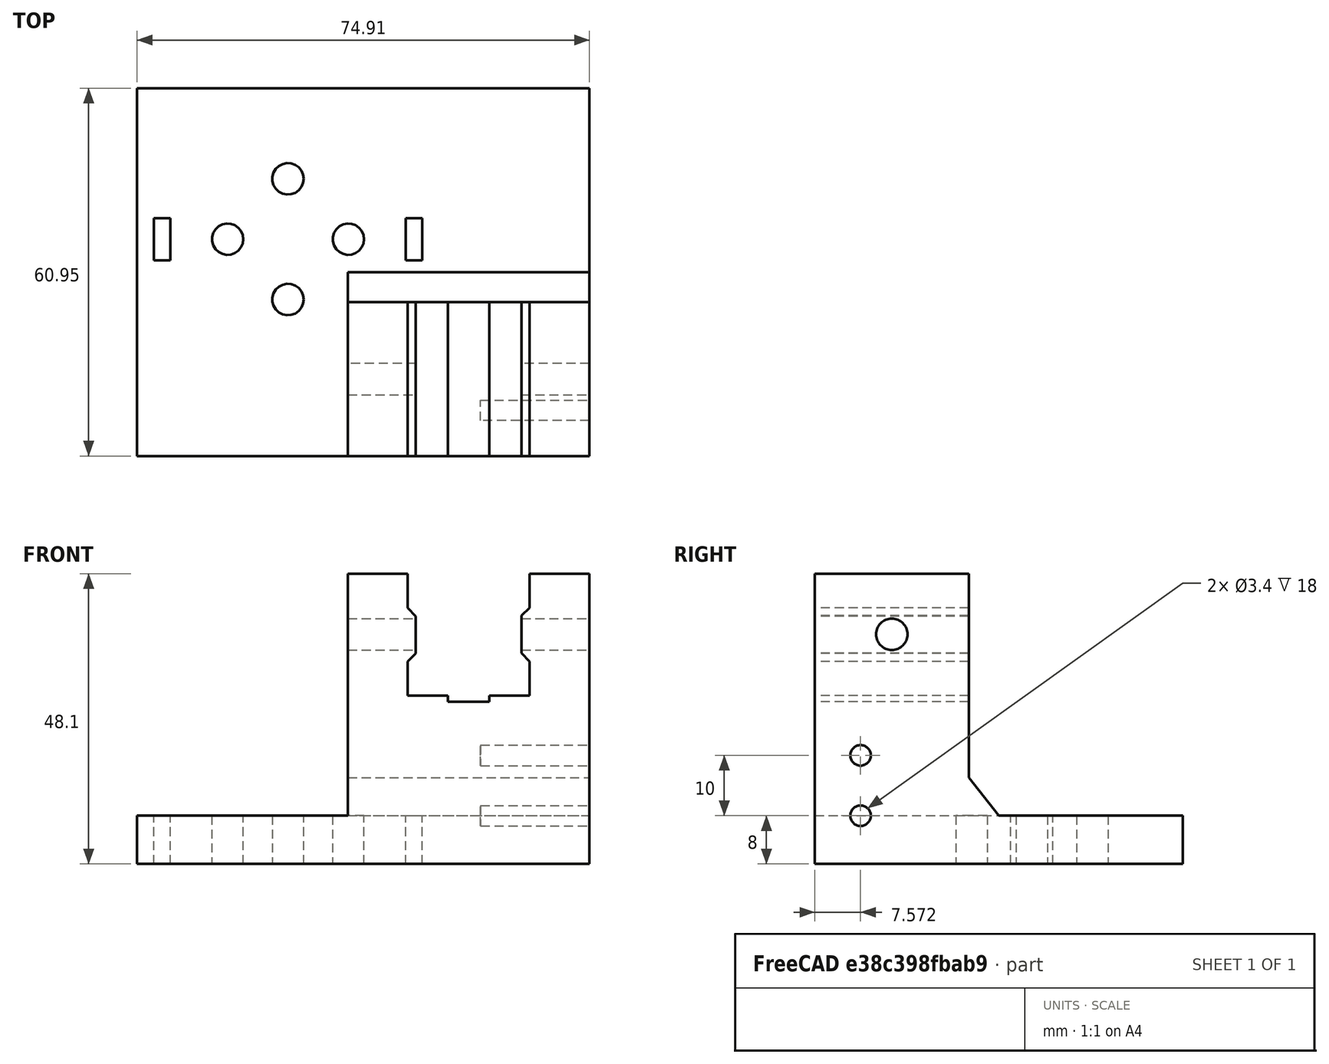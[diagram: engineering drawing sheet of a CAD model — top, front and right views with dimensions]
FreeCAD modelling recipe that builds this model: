
FCSTD DOCUMENT  (FreeCAD 1.0R39109 (Git))
Label: plotter_x_axis_idler
License: All rights reserved
LicenseURL: https://en.wikipedia.org/wiki/All_rights_reserved
objects: Sketcher::SketchObject×12, PartDesign::Pad×3, PartDesign::Pocket×3, PartDesign::Body×2, Mesh::Feature×1, PartDesign::LinearPattern×1, Part::Mirroring×1, PartDesign::FeatureBase×1
note: 49 computed .brp shape members not serialized (recipe doc carries the construction recipe); baked Part::Feature solids carry a one-line shape summary decoded from their .brp

FEATURE [Mesh::Feature] _0x20_v_slot  label="20x20_v-slot"
  Placement = pos=(29.9,-56,38) rot=(0,0,1;0rad)
FEATURE [Sketcher::SketchObject] Sketch007
  ArcFitTolerance = 1e-06
  AttachmentSupport = -> [XY_Plane001]
  FullyConstrained = false
  MakeInternals = false
  MapMode = 5
  sketch-geometry (19):
    g0: LineSegment StartX=49.9144 StartY=35.9499 StartZ=0 EndX=-25 EndY=35.9499 EndZ=0
    g1: LineSegment StartX=-25 StartY=35.9499 StartZ=0 EndX=-25 EndY=-25 EndZ=0
    g2: LineSegment StartX=-25 StartY=-25 StartZ=0 EndX=49.9144 EndY=-25 EndZ=0
    g3: LineSegment StartX=49.9144 StartY=-25 StartZ=0 EndX=49.9144 EndY=35.9499 EndZ=0
    g4: Circle CenterX=0 CenterY=10 CenterZ=0 NormalX=0 NormalY=0 NormalZ=1 AngleXU=0 Radius=2.6
    g5: Circle CenterX=10 CenterY=0 CenterZ=0 NormalX=0 NormalY=0 NormalZ=1 AngleXU=0 Radius=2.6
    g6: Circle CenterX=-10 CenterY=0 CenterZ=0 NormalX=0 NormalY=0 NormalZ=1 AngleXU=0 Radius=2.6
    g7: Circle CenterX=0 CenterY=-10 CenterZ=0 NormalX=0 NormalY=0 NormalZ=1 AngleXU=0 Radius=2.6
    g8: LineSegment [constr] StartX=43.4104 StartY=34.4675 StartZ=0 EndX=43.4104 EndY=14.8633 EndZ=0
    g9: LineSegment StartX=22.25 StartY=-3.5 StartZ=0 EndX=22.25 EndY=3.5 EndZ=0
    g10: LineSegment StartX=22.25 StartY=3.5 StartZ=0 EndX=19.5 EndY=3.5 EndZ=0
    g11: LineSegment StartX=19.5 StartY=3.5 StartZ=0 EndX=19.5 EndY=-3.5 EndZ=0
    g12: LineSegment StartX=19.5 StartY=-3.5 StartZ=0 EndX=22.25 EndY=-3.5 EndZ=0
    g13: GeomPoint [constr] X=20.875 Y=0 Z=0
    g14: LineSegment StartX=-19.5 StartY=-3.5 StartZ=0 EndX=-19.5 EndY=3.5 EndZ=0
    g15: LineSegment StartX=-19.5 StartY=3.5 StartZ=0 EndX=-22.25 EndY=3.5 EndZ=0
    g16: LineSegment StartX=-22.25 StartY=3.5 StartZ=0 EndX=-22.25 EndY=-3.5 EndZ=0
    g17: LineSegment StartX=-22.25 StartY=-3.5 StartZ=0 EndX=-19.5 EndY=-3.5 EndZ=0
    g18: GeomPoint [constr] X=-20.875 Y=0 Z=0
  constraints (49):
    c: Coincident(g0,g1)
    c: Coincident(g1,g2)
    c: Coincident(g2,g3)
    c: Coincident(g3,g0)
    c: Horizontal(g0)
    c: Horizontal(g2)
    c: Vertical(g1)
    c: Vertical(g3)
    c: Diameter(g4) = 5.2
    c: PointOnObject(g4,g-2)
    c: Diameter(g5) = 5.2
    c: PointOnObject(g5,g-1)
    c: Diameter(g6) = 5.2
    c: Diameter(g7) = 5.2
    c: PointOnObject(g7,g-2)
    c: DistanceX(g-1,g5) = 10
    c: DistanceY(g7,g-1) = 10
    c: DistanceY(g-1,g4) = 10
    c: DistanceX(g6,g-1) = 10
    c: PointOnObject(g6,g-1)
    c: Vertical(g8)
    c: DistanceY(g1,g-1) = 25
    c: DistanceX(g1,g-1) = 25
    c: Coincident(g9,g10)
    c: Coincident(g10,g11)
    c: Coincident(g11,g12)
    c: Coincident(g12,g9)
    c: Vertical(g9)
    c: Vertical(g11)
    c: Horizontal(g10)
    c: Horizontal(g12)
    c: Symmetric(g11,g9,g13)
    c: PointOnObject(g13,g-1)
    c: Coincident(g14,g15)
    c: Coincident(g15,g16)
    c: Coincident(g16,g17)
    c: Coincident(g17,g14)
    c: Vertical(g14)
    c: Vertical(g16)
    c: Horizontal(g15)
    c: Horizontal(g17)
    c: Symmetric(g16,g14,g18)
    c: PointOnObject(g18,g-1)
    c: Equal(g11,g14)
    c: DistanceY(g11,g11) = 7
    c: Equal(g10,g15)
    c: DistanceX(g15,g15) = 2.75
    c: DistanceX(g14,g11) = 39
    c: DistanceX(g14,g-1) = 19.5
FEATURE [PartDesign::Pad] Pad005
  Direction = (0,0,1)
  Length = 8
  Length2 = 10
  Profile = -> Sketch007
  ReferenceAxis = -> Sketch007 [N_Axis]
  Refine = true
  Suppressed = false
  Type = 0
FEATURE [Sketcher::SketchObject] Sketch009
  ArcFitTolerance = 1e-06
  AttachmentSupport = -> [Pad005]
  ExternalGeometry = -> [Pad005]
  FullyConstrained = false
  MakeInternals = false
  MapMode = 5
  Placement = pos=(0,0,8) rot=(0,0,1;0rad)
  sketch-geometry (4):
    g0: LineSegment StartX=49.9144 StartY=35.9499 StartZ=0 EndX=9.91437 EndY=35.9499 EndZ=0
    g1: LineSegment StartX=9.91437 StartY=35.9499 StartZ=0 EndX=9.91437 EndY=10.4651 EndZ=0
    g2: LineSegment StartX=9.91437 StartY=10.4651 StartZ=0 EndX=49.9144 EndY=10.4651 EndZ=0
    g3: LineSegment StartX=49.9144 StartY=10.4651 StartZ=0 EndX=49.9144 EndY=35.9499 EndZ=0
  constraints (10):
    c: Coincident(g0,g1)
    c: Coincident(g1,g2)
    c: Coincident(g2,g3)
    c: Coincident(g3,g0)
    c: Horizontal(g0)
    c: Horizontal(g2)
    c: Vertical(g1)
    c: Vertical(g3)
    c: Distance(g1,g3) = 40
    c: Coincident(g0,g-4)
FEATURE [PartDesign::Pad] Pad006
  BaseFeature = -> Pad005
  Direction = (0,0,1)
  Length = 40.1
  Length2 = 10
  Profile = -> Sketch009
  ReferenceAxis = -> Sketch009 [N_Axis]
  Refine = true
  Suppressed = false
  Type = 0
FEATURE [Sketcher::SketchObject] Sketch010
  ArcFitTolerance = 1e-06
  AttachmentSupport = -> [Pad006]
  ExternalGeometry = -> [Pad006]
  FullyConstrained = false
  MakeInternals = false
  MapMode = 5
  Placement = pos=(0,10.4651,0) rot=(1,0,0;1.5708rad)
  sketch-geometry (17):
    g0: LineSegment [constr] StartX=29.9144 StartY=48.1 StartZ=0 EndX=29.9144 EndY=14.8286 EndZ=0
    g1: LineSegment StartX=19.8144 StartY=48.1 StartZ=0 EndX=19.8144 EndY=42.4266 EndZ=0
    g2: LineSegment StartX=19.8144 StartY=42.4266 StartZ=0 EndX=21.1404 EndY=41.0594 EndZ=0
    g3: LineSegment StartX=21.1404 StartY=41.0594 StartZ=0 EndX=21.1404 EndY=34.8594 EndZ=0
    g4: LineSegment StartX=21.1404 StartY=34.8594 StartZ=0 EndX=19.8144 EndY=33.5734 EndZ=0
    g5: LineSegment StartX=19.8144 StartY=33.5734 StartZ=0 EndX=19.8144 EndY=27.9 EndZ=0
    g6: LineSegment StartX=19.8144 StartY=27.9 StartZ=0 EndX=26.496 EndY=27.9 EndZ=0
    g7: LineSegment StartX=26.496 StartY=27.9 StartZ=0 EndX=26.496 EndY=26.9 EndZ=0
    g8: LineSegment StartX=26.496 StartY=26.9 StartZ=0 EndX=33.3327 EndY=26.9 EndZ=0
    g9: LineSegment StartX=33.3327 StartY=26.9 StartZ=0 EndX=33.3327 EndY=27.9 EndZ=0
    g10: LineSegment StartX=33.3327 StartY=27.9 StartZ=0 EndX=40.0144 EndY=27.9 EndZ=0
    g11: LineSegment StartX=40.0144 StartY=27.9 StartZ=0 EndX=40.0144 EndY=33.5734 EndZ=0
    g12: LineSegment StartX=40.0144 StartY=33.5734 StartZ=0 EndX=38.6893 EndY=34.9653 EndZ=0
    g13: LineSegment StartX=38.6893 StartY=34.9653 StartZ=0 EndX=38.6893 EndY=41.1653 EndZ=0
    g14: LineSegment StartX=38.6893 StartY=41.1653 StartZ=0 EndX=40.0144 EndY=42.4266 EndZ=0
    g15: LineSegment StartX=40.0144 StartY=42.4266 StartZ=0 EndX=40.0144 EndY=48.1 EndZ=0
    g16: LineSegment StartX=40.0144 StartY=48.1 StartZ=0 EndX=19.8144 EndY=48.1 EndZ=0
  constraints (46):
    c: Symmetric(g-3,g-3,g0)
    c: Vertical(g0)
    c: PointOnObject(g1,g-3)
    c: Vertical(g1)
    c: Coincident(g1,g2)
    c: Coincident(g2,g3)
    c: Vertical(g3)
    c: Coincident(g3,g4)
    c: Coincident(g4,g5)
    c: Vertical(g5)
    c: Coincident(g5,g6)
    c: Coincident(g6,g7)
    c: Vertical(g7)
    c: Coincident(g7,g8)
    c: Horizontal(g8)
    c: Coincident(g8,g9)
    c: Vertical(g9)
    c: Coincident(g9,g10)
    c: Coincident(g10,g11)
    c: Vertical(g11)
    c: Coincident(g11,g12)
    c: Coincident(g12,g13)
    c: Vertical(g13)
    c: Coincident(g13,g14)
    c: Coincident(g14,g15)
    c: PointOnObject(g15,g-3)
    c: Vertical(g15)
    c: Coincident(g15,g16)
    c: Coincident(g16,g1)
    c: Equal(g13,g3)
    c: Equal(g15,g1)
    c: Equal(g1,g5)
    c: Equal(g5,g11)
    c: Equal(g6,g10)
    c: Equal(g9,g7)
    c: DistanceY(g3,g3) = 6.2
    c: DistanceX(g4,g11) = 20.2
    c: DistanceX(g11,g14) = 0
    c: DistanceX(g1,g4) = 0
    c: DistanceY(g10,g15) = 20.2
    c: DistanceY(g10,g5) = 0
    c: Parallel(g6,g10)
    c: DistanceY(g9,g9) = 1
    c: DistanceX(g1,g0) = 10.1
    c: Perpendicular(g4,g2)
    c: Perpendicular(g12,g14)
FEATURE [PartDesign::Pocket] Pocket004
  BaseFeature = -> Pad006
  Direction = (0,1,-2e-16)
  Length = 50
  Length2 = 5
  Profile = -> Sketch010
  ReferenceAxis = -> Sketch010 [N_Axis]
  Refine = true
  Suppressed = false
  Type = 0
FEATURE [Sketcher::SketchObject] Sketch011
  ArcFitTolerance = 1e-06
  AttachmentSupport = -> [Pocket004]
  ExternalGeometry = -> [Pocket004]
  FullyConstrained = true
  MakeInternals = false
  MapMode = 5
  Placement = pos=(0,0,8) rot=(0,0,1;0rad)
  sketch-geometry (8):
    g0: LineSegment StartX=15.3144 StartY=10.4651 StartZ=0 EndX=15.3144 EndY=-25 EndZ=0
    g1: LineSegment StartX=15.3144 StartY=-25 StartZ=0 EndX=19.8144 EndY=-25 EndZ=0
    g2: LineSegment StartX=19.8144 StartY=-25 StartZ=0 EndX=19.8144 EndY=-3.5 EndZ=0
    g3: LineSegment StartX=19.8144 StartY=-3.5 StartZ=0 EndX=19.5 EndY=-3.5 EndZ=0
    g4: LineSegment StartX=19.5 StartY=-3.5 StartZ=0 EndX=19.5 EndY=3.5 EndZ=0
    g5: LineSegment StartX=19.5 StartY=3.5 StartZ=0 EndX=19.8144 EndY=3.5 EndZ=0
    g6: LineSegment StartX=19.8144 StartY=3.5 StartZ=0 EndX=19.8144 EndY=10.4651 EndZ=0
    g7: LineSegment StartX=19.8144 StartY=10.4651 StartZ=0 EndX=15.3144 EndY=10.4651 EndZ=0
  constraints (21):
    c: Vertical(g0)
    c: Coincident(g0,g1)
    c: Coincident(g1,g2)
    c: Vertical(g2)
    c: Coincident(g2,g3)
    c: Coincident(g3,g4)
    c: Coincident(g4,g5)
    c: Horizontal(g5)
    c: Coincident(g5,g6)
    c: Vertical(g6)
    c: Coincident(g6,g7)
    c: Coincident(g7,g0)
    c: Coincident(g4,g-3)
    c: Coincident(g3,g-4)
    c: Parallel(g3,g-1)
    c: Equal(g1,g7)
    c: Parallel(g7,g1)
    c: PointOnObject(g1,g-6)
    c: Coincident(g6,g-5)
    c: DistanceY(g0,g-5) = 0
    c: DistanceX(g1,g1) = 4.5
FEATURE [Sketcher::SketchObject] Sketch012
  ArcFitTolerance = 1e-06
  FullyConstrained = false
  MakeInternals = false
  MapMode = 5
  Placement = pos=(49.9144,0,0) rot=(0.57735,0.57735,0.57735;2.0944rad)
  sketch-geometry (1):
    g0: Circle CenterX=28.4297 CenterY=38.1 CenterZ=0 NormalX=0 NormalY=0 NormalZ=1 AngleXU=0 Radius=2.7
  constraints (2):
    c: Diameter(g0) = 5.4
    c: DistanceY(g0,g-3) = 10
FEATURE [Sketcher::SketchObject] Sketch013
  ArcFitTolerance = 1e-06
  FullyConstrained = true
  MakeInternals = false
  MapMode = 5
  Placement = pos=(0,20.8055,0) rot=(1,0,0;1.5708rad)
  sketch-geometry (8):
    g0: LineSegment StartX=40.0144 StartY=48.1 StartZ=0 EndX=40.0144 EndY=42.4266 EndZ=0
    g1: LineSegment StartX=40.0144 StartY=42.4266 StartZ=0 EndX=38.6893 EndY=41.1653 EndZ=0
    g2: LineSegment StartX=38.6893 StartY=41.1653 StartZ=0 EndX=38.6893 EndY=34.9653 EndZ=0
    g3: LineSegment StartX=38.6893 StartY=34.9653 StartZ=0 EndX=40.0144 EndY=33.5734 EndZ=0
    g4: LineSegment StartX=40.0144 StartY=33.5734 StartZ=0 EndX=40.0144 EndY=27.9 EndZ=0
    g5: LineSegment StartX=40.0144 StartY=27.9 StartZ=0 EndX=49.9144 EndY=28.05 EndZ=0
    g6: LineSegment StartX=49.9144 StartY=28.05 StartZ=0 EndX=49.9144 EndY=48.1 EndZ=0
    g7: LineSegment StartX=49.9144 StartY=48.1 StartZ=0 EndX=40.0144 EndY=48.1 EndZ=0
  constraints (16):
    c: Coincident(g-4,g0)
    c: Coincident(g0,g-5)
    c: Coincident(g0,g1)
    c: Coincident(g1,g-6)
    c: Coincident(g1,g2)
    c: Coincident(g2,g-7)
    c: Coincident(g2,g3)
    c: Coincident(g3,g-8)
    c: Coincident(g3,g4)
    c: Coincident(g4,g-8)
    c: Coincident(g4,g5)
    c: Symmetric(g-9,g-9,g5)
    c: Coincident(g5,g6)
    c: Coincident(g6,g-9)
    c: Coincident(g6,g7)
    c: Coincident(g7,g0)
FEATURE [Sketcher::SketchObject] Sketch014
  ArcFitTolerance = 1e-06
  FullyConstrained = false
  MakeInternals = false
  MapMode = 5
  Placement = pos=(19.8144,0,0) rot=(0.57735,0.57735,0.57735;2.0944rad)
  sketch-geometry (10):
    g0: Circle CenterX=-1.26785 CenterY=38.1 CenterZ=0 NormalX=0 NormalY=0 NormalZ=1 AngleXU=0 Radius=12
    g1: LineSegment [constr] StartX=14.2321 StartY=22.6 StartZ=0 EndX=14.2321 EndY=53.6 EndZ=0
    g2: LineSegment [constr] StartX=14.2321 StartY=53.6 StartZ=0 EndX=-16.7679 EndY=53.6 EndZ=0
    g3: LineSegment [constr] StartX=-16.7679 StartY=53.6 StartZ=0 EndX=-16.7679 EndY=22.6 EndZ=0
    g4: LineSegment [constr] StartX=-16.7679 StartY=22.6 StartZ=0 EndX=14.2321 EndY=22.6 EndZ=0
    g5: GeomPoint [constr] X=-1.26785 Y=38.1 Z=0
    g6: Circle CenterX=-16.7679 CenterY=53.6 CenterZ=0 NormalX=0 NormalY=0 NormalZ=1 AngleXU=0 Radius=1.6
    g7: Circle CenterX=14.2321 CenterY=53.6 CenterZ=0 NormalX=0 NormalY=0 NormalZ=1 AngleXU=0 Radius=1.6
    g8: Circle CenterX=14.2321 CenterY=22.6 CenterZ=0 NormalX=0 NormalY=0 NormalZ=1 AngleXU=0 Radius=1.6
    g9: Circle CenterX=-16.7679 CenterY=22.6 CenterZ=0 NormalX=0 NormalY=0 NormalZ=1 AngleXU=0 Radius=1.6
  constraints (22):
    c: Diameter(g0) = 24
    c: Coincident(g1,g2)
    c: Coincident(g2,g3)
    c: Coincident(g3,g4)
    c: Coincident(g4,g1)
    c: Vertical(g1)
    c: Vertical(g3)
    c: Horizontal(g2)
    c: Horizontal(g4)
    c: Symmetric(g3,g1,g5)
    c: Coincident(g5,g0)
    c: Equal(g2,g3)
    c: DistanceX(g2,g2) = 31
    c: Coincident(g6,g2)
    c: Coincident(g7,g1)
    c: Coincident(g8,g1)
    c: Coincident(g9,g3)
    c: Diameter(g9) = 3.2
    c: Equal(g9,g6)
    c: Equal(g6,g7)
    c: Equal(g7,g8)
    c: DistanceY(g0,g-3) = 10
FEATURE [Sketcher::SketchObject] Sketch015
  ArcFitTolerance = 1e-06
  ExternalGeometry = -> [Sketch007]
  FullyConstrained = true
  MakeInternals = false
  MapMode = 5
  Placement = pos=(0,20.8055,0) rot=(1,0,0;1.5708rad)
  sketch-geometry (7):
    g0: GeomPoint [constr] X=34.8644 Y=8 Z=0
    g1: GeomPoint X=34.8644 Y=8 Z=0
    g2: LineSegment StartX=19.8144 StartY=16 StartZ=0 EndX=19.8144 EndY=0 EndZ=0
    g3: LineSegment StartX=19.8144 StartY=0 StartZ=0 EndX=49.9144 EndY=0 EndZ=0
    g4: LineSegment StartX=49.9144 StartY=0 StartZ=0 EndX=49.9144 EndY=16 EndZ=0
    g5: LineSegment StartX=49.9144 StartY=16 StartZ=0 EndX=19.8144 EndY=16 EndZ=0
    g6: GeomPoint [constr] X=34.8644 Y=8 Z=0
  constraints (13):
    c: Symmetric(g-4,g-4,g0)
    c: Coincident(g1,g0)
    c: Coincident(g2,g3)
    c: Coincident(g3,g4)
    c: Coincident(g4,g5)
    c: Coincident(g5,g2)
    c: Vertical(g2)
    c: Vertical(g4)
    c: Horizontal(g3)
    c: Horizontal(g5)
    c: Symmetric(g4,g2,g6)
    c: Symmetric(g-4,g-4,g6)
    c: Coincident(g3,g-6)
FEATURE [Sketcher::SketchObject] Sketch016
  ArcFitTolerance = 1e-06
  FullyConstrained = true
  MakeInternals = false
  MapMode = 5
  Placement = pos=(49.9144,0,0) rot=(0.57735,0.57735,0.57735;2.0944rad)
  sketch-geometry (2):
    g0: Circle CenterX=28.3777 CenterY=8 CenterZ=0 NormalX=0 NormalY=0 NormalZ=1 AngleXU=0 Radius=1.7
    g1: GeomPoint X=35.9499 Y=8 Z=0
  constraints (4):
    c: PointOnObject(g1,g-3)
    c: DistanceY(g1,g-4) = 0
    c: Symmetric(g-4,g1,g0)
    c: Diameter(g0) = 3.4
FEATURE [PartDesign::Pocket] Pocket008
  BaseFeature = -> Pocket004
  Direction = (-1,0,0)
  Length = 18
  Length2 = 5
  Profile = -> Sketch016
  ReferenceAxis = -> Sketch016 [N_Axis]
  Refine = true
  Suppressed = false
  Type = 0
FEATURE [PartDesign::LinearPattern] LinearPattern
  BaseFeature = -> Pocket008
  Direction = -> Sketch016 [V_Axis]
  Length = 10
  Mode = 0
  Occurrences = 2
  Offset = 10
  Originals = -> [Pocket008]
  Refine = true
  Suppressed = false
  TransformMode = 0
FEATURE [PartDesign::Body] Body001  label="XPlateNew"
  AllowCompound = false
  Group = -> [Sketch007,Pad005,Sketch009,Pad006,Sketch010,Pocket004,Sketch011,Sketch012,Sketch013,Sketch014,Sketch015,Sketch016,Pocket008,LinearPattern]
  Origin = -> Origin001
  Tip = -> LinearPattern
FEATURE [Part::Mirroring] Part__Mirroring  label="XPlateNew (Mirror #1)"
  Base = (12.4572,3.8147e-06,24.05)
  Normal = (0,1,-1.19209e-07)
  Placement = pos=(0,18,0) rot=(0,0,1;0rad)
  Source = -> Body001
FEATURE [PartDesign::FeatureBase] BaseFeature
  BaseFeature = -> Part__Mirroring
  Suppressed = false
FEATURE [Sketcher::SketchObject] Sketch
  ArcFitTolerance = 1e-06
  AttachmentSupport = -> [BaseFeature]
  ExternalGeometry = -> [BaseFeature]
  FullyConstrained = true
  MakeInternals = false
  MapMode = 5
  Placement = pos=(0,-10.4651,2.49507e-06) rot=(0,0.707107,0.707107;3.14159rad)
  sketch-geometry (10):
    g0: LineSegment StartX=-49.9144 StartY=8 StartZ=0 EndX=-49.9144 EndY=48.1 EndZ=0
    g1: LineSegment StartX=-49.9144 StartY=48.1 StartZ=0 EndX=-40.0144 EndY=48.1 EndZ=0
    g2: LineSegment StartX=-40.0144 StartY=48.1 StartZ=0 EndX=-40.0144 EndY=42.4266 EndZ=0
    g3: LineSegment StartX=-40.0144 StartY=42.4266 StartZ=0 EndX=-38.6893 EndY=41.1653 EndZ=0
    g4: LineSegment StartX=-38.6893 StartY=41.1653 StartZ=0 EndX=-38.6893 EndY=34.9653 EndZ=0
    g5: LineSegment StartX=-38.6893 StartY=34.9653 StartZ=0 EndX=-40.0144 EndY=33.5734 EndZ=0
    g6: LineSegment StartX=-40.0144 StartY=33.5734 StartZ=0 EndX=-40.0144 EndY=27.9 EndZ=0
    g7: LineSegment StartX=-40.0144 StartY=27.9 StartZ=0 EndX=-33.3327 EndY=27.9 EndZ=0
    g8: LineSegment StartX=-33.3327 StartY=27.9 StartZ=0 EndX=-33.3327 EndY=8 EndZ=0
    g9: LineSegment StartX=-33.3327 StartY=8 StartZ=0 EndX=-49.9144 EndY=8 EndZ=0
  constraints (21):
    c: Coincident(g-11,g0)
    c: Coincident(g0,g-10)
    c: Coincident(g0,g1)
    c: Coincident(g1,g-4)
    c: Coincident(g1,g2)
    c: Coincident(g2,g-5)
    c: Coincident(g2,g3)
    c: Coincident(g3,g-6)
    c: Coincident(g3,g4)
    c: Coincident(g4,g-7)
    c: Coincident(g4,g5)
    c: Coincident(g5,g-8)
    c: Coincident(g5,g6)
    c: Coincident(g6,g-9)
    c: Coincident(g6,g7)
    c: Coincident(g7,g-9)
    c: Coincident(g7,g8)
    c: PointOnObject(g8,g-11)
    c: Vertical(g8)
    c: Coincident(g8,g9)
    c: Coincident(g9,g0)
FEATURE [Sketcher::SketchObject] Sketch017
  ArcFitTolerance = 1e-06
  AttachmentSupport = -> [BaseFeature]
  ExternalGeometry = -> [BaseFeature,Sketch]
  FullyConstrained = true
  MakeInternals = false
  MapMode = 5
  Placement = pos=(49.9144,0,0) rot=(0.57735,0.57735,0.57735;2.0944rad)
  sketch-geometry (2):
    g0: LineSegment [constr] StartX=-35.9499 StartY=28.05 StartZ=0 EndX=-10.4651 EndY=28.05 EndZ=0
    g1: Circle CenterX=-23.2075 CenterY=38.075 CenterZ=0 NormalX=0 NormalY=0 NormalZ=1 AngleXU=0 Radius=2.6
  constraints (5):
    c: PointOnObject(g0,g-3)
    c: Symmetric(g-4,g-4,g0)
    c: Horizontal(g0)
    c: Diameter(g1) = 5.2
    c: Symmetric(g-4,g0,g1)
FEATURE [PartDesign::Pocket] Pocket
  BaseFeature = -> BaseFeature
  Direction = (-1,0,0)
  Length = 10000
  Length2 = 5
  Profile = -> Sketch017
  ReferenceAxis = -> Sketch017 [N_Axis]
  Refine = true
  Suppressed = false
  Type = 0
FEATURE [Sketcher::SketchObject] Sketch020
  ArcFitTolerance = 1e-06
  AttachmentSupport = -> [Pocket]
  ExternalGeometry = -> [Pocket]
  FullyConstrained = false
  MakeInternals = false
  MapMode = 5
  Placement = pos=(9.91437,0,0) rot=(0.57735,-0.57735,-0.57735;2.0944rad)
  sketch-geometry (3):
    g0: LineSegment StartX=10.4651 StartY=8 StartZ=0 EndX=5.50359 EndY=8 EndZ=0
    g1: LineSegment StartX=5.50359 StartY=8 StartZ=0 EndX=10.4651 EndY=14.3015 EndZ=0
    g2: LineSegment StartX=10.4651 StartY=14.3015 StartZ=0 EndX=10.4651 EndY=8 EndZ=0
  constraints (6):
    c: Horizontal(g0)
    c: Coincident(g0,g1)
    c: Coincident(g1,g2)
    c: Coincident(g2,g0)
    c: PointOnObject(g1,g-3)
    c: Coincident(g0,g-3)
FEATURE [PartDesign::Pad] Pad009
  BaseFeature = -> Pocket
  Direction = (-1,0,0)
  Length = 40
  Length2 = 10
  Profile = -> Sketch020
  ReferenceAxis = -> Sketch020 [N_Axis]
  Refine = true
  Reversed = true
  Suppressed = false
  Type = 0
FEATURE [PartDesign::Body] Body  label="XPlateNewIdler"
  AllowCompound = false
  BaseFeature = -> Part__Mirroring
  Group = -> [BaseFeature,Sketch,Sketch017,Pocket,Sketch020,Pad009]
  Origin = -> Origin
  Tip = -> Pad009
